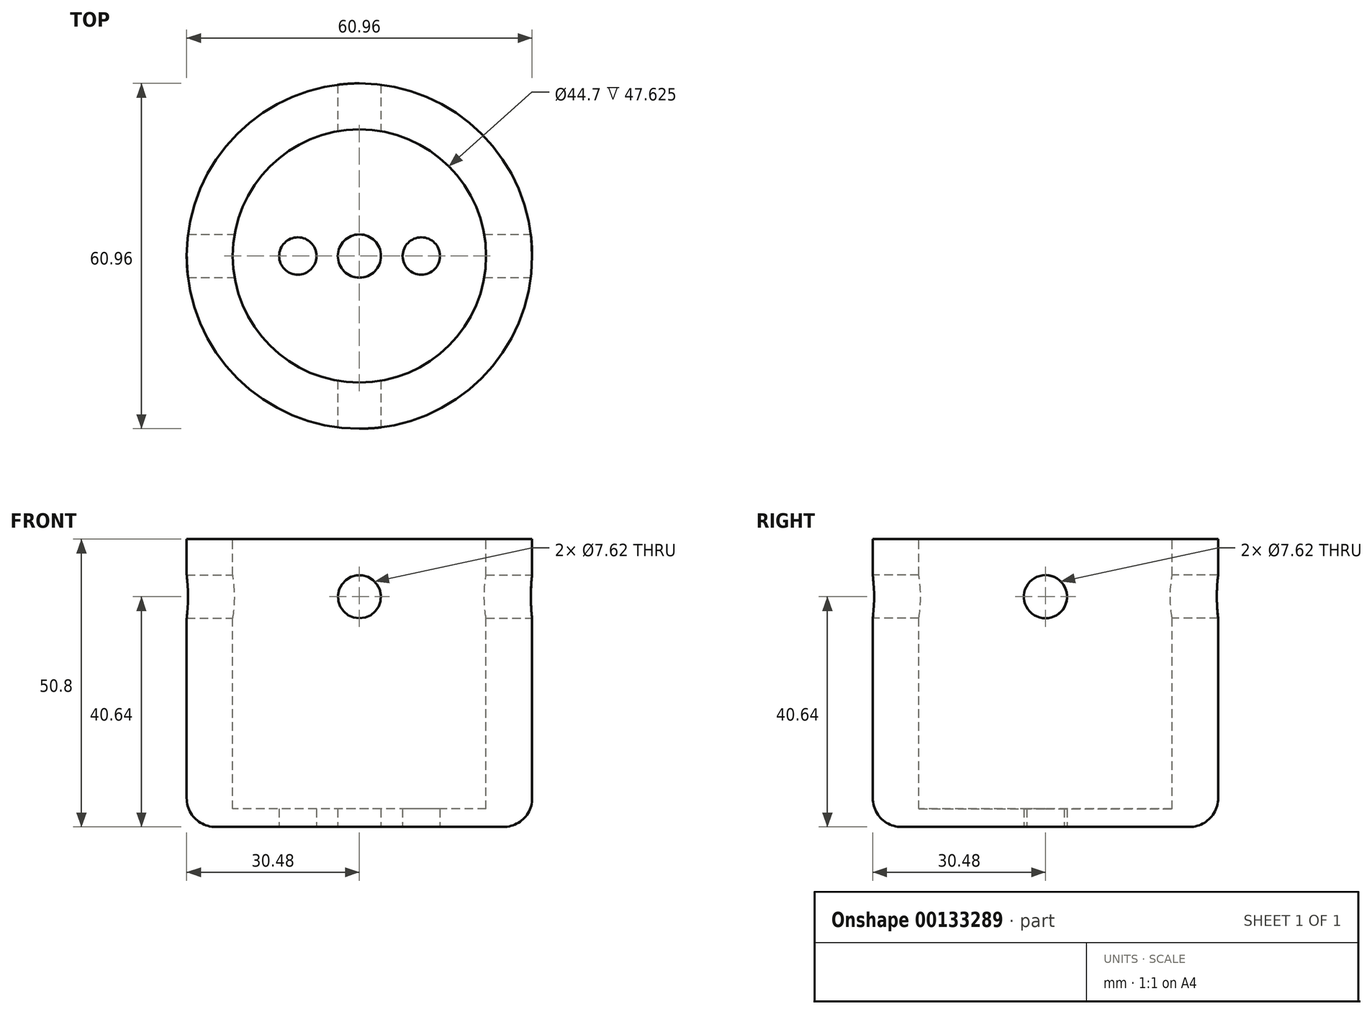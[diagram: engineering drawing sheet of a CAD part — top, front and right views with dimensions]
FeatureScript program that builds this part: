
annotation { "Feature Type Name" : "Feature", "Feature Type Description" : "" }
export const myFeature = defineFeature(function(context is Context, id is Id, definition is map)
    precondition{}
    {
        {
            var Q0;
            Q0=qCreatedBy(makeId("Top.planeOp"),FACE);
            var sketch = newSketch(context, id + "F0", { "sketchPlane" : qUnion([Q0])});
            skCircle(sketch, "E0", {"center": v(0, 0) * mm, "radius": 30.48 * mm});
            skSolve(sketch);
        }
        {
            var Q0;
            Q0=qSketchRegion(id+"F0",true);
            extrude(context, id + "F1", {"entities" : qUnion([Q0]), "oppositeDirection" : true, "depth" : 50.8 * mm});
        }
        {
            var Q0;
            Q0=makeQuery(id+"F1.opExtrude","CAP_FACE",FACE,{"disambiguationData":[OSD([sQuery(id+"F0.wireOp",EDGE,"E0")])],"isStart":false});
            var sketch = newSketch(context, id + "F2", { "sketchPlane" : qUnion([Q0])});
            skCircle(sketch, "E1", {"center": v(0, 0) * mm, "radius": 3.8 * mm});
            skSolve(sketch);
        }
        {
            var Q0;
            Q0=qSketchRegion(id+"F2",true);
            extrude(context, id + "F3", {"entities" : qUnion([Q0]), "operationType" : NewBodyOperationType.REMOVE, "endBound" : BoundingType.THROUGH_ALL, "oppositeDirection" : true, "depth" : 38.1 * mm});
        }
        {
            var Q0;
            Q0=qCreatedBy(makeId("Right.planeOp"),FACE);
            var sketch = newSketch(context, id + "F4", { "sketchPlane" : qUnion([Q0])});
            skLineSegment(sketch, "E2", {"start": v(0, 0) * mm, "end": v(0, -74.59) * mm, "construction": true});
            skCircle(sketch, "E3", {"center": v(0, -10.16) * mm, "radius": 3.81 * mm});
            skSolve(sketch);
        }
        {
            var Q0;
            Q0=qSketchRegion(id+"F4",true);
            extrude(context, id + "F5", {"entities" : qUnion([Q0]), "operationType" : NewBodyOperationType.REMOVE, "endBound" : BoundingType.THROUGH_ALL, "oppositeDirection" : true, "depth" : 25.4 * mm, "hasSecondDirection" : true, "secondDirectionBound" : BoundingType.THROUGH_ALL, "secondDirectionOppositeDirection" : false, "secondDirectionDepth" : 25.4 * mm});
        }
        {
            var Q0;
            Q0=qCreatedBy(makeId("Front.planeOp"),FACE);
            var sketch = newSketch(context, id + "F6", { "sketchPlane" : qUnion([Q0])});
            skLineSegment(sketch, "E4", {"start": v(0, 0) * mm, "end": v(0, -36.04) * mm, "construction": true});
            skCircle(sketch, "E5", {"center": v(0, -10.16) * mm, "radius": 3.81 * mm});
            skSolve(sketch);
        }
        {
            var Q0;
            Q0=qSketchRegion(id+"F6",true);
            extrude(context, id + "F7", {"entities" : qUnion([Q0]), "operationType" : NewBodyOperationType.REMOVE, "endBound" : BoundingType.THROUGH_ALL, "oppositeDirection" : true, "depth" : 25.4 * mm, "hasSecondDirection" : true, "secondDirectionBound" : BoundingType.THROUGH_ALL, "secondDirectionOppositeDirection" : false, "secondDirectionDepth" : 25.4 * mm});
        }
        {
            var Q0;
            Q0=makeQuery(id+"F1.opExtrude","CAP_FACE",FACE,{"disambiguationData":[OSD([sQuery(id+"F0.wireOp",EDGE,"E0")])],"isStart":false});
            var sketch = newSketch(context, id + "F8", { "sketchPlane" : qUnion([Q0])});
            skCircle(sketch, "E6", {"center": v(10.92, 0) * mm, "radius": 3.3 * mm});
            skCircle(sketch, "E7", {"center": v(-10.87, 0) * mm, "radius": 3.3 * mm});
            skSolve(sketch);
        }
        {
            var Q0;
            Q0=qSketchRegion(id+"F8",true);
            extrude(context, id + "F9", {"entities" : qUnion([Q0]), "operationType" : NewBodyOperationType.REMOVE, "endBound" : BoundingType.THROUGH_ALL, "oppositeDirection" : true, "depth" : 31.86 * mm});
        }
        {
            var Q0;
            Q0=makeQuery(id+"F1.opExtrude","CAP_FACE",FACE,{"disambiguationData":[OSD([sQuery(id+"F0.wireOp",EDGE,"E0")])],"isStart":true});
            var sketch = newSketch(context, id + "F10", { "sketchPlane" : qUnion([Q0])});
            skCircle(sketch, "E8", {"center": v(0, 0) * mm, "radius": 22.35 * mm});
            skSolve(sketch);
        }
        {
            var Q0;
            Q0=qSketchRegion(id+"F10",true);
            extrude(context, id + "F11", {"entities" : qUnion([Q0]), "operationType" : NewBodyOperationType.REMOVE, "oppositeDirection" : true, "depth" : 47.62 * mm});
        }
        {
            var Q0;
            Q0=makeQuery(id+"F1.opExtrude","CAP_EDGE",EDGE,{"disambiguationData":[OSD([sQuery(id+"F0.wireOp",EDGE,"E0")])],"isStart":false});
            fillet(context, id + "F12", {"entities" : qUnion([Q0]), "radius" : 5.08 * mm, "tangentPropagation" : true, "allowEdgeOverflow" : false});
        }
    });
